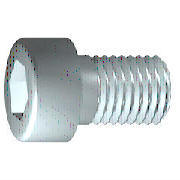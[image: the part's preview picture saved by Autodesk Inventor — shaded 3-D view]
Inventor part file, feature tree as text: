
AUTODESK INVENTOR PART (.ipt)
format: ipt  version: 2020 (Build 240168000, 168)  size: 191,488 bytes
history: native  units: mm (DEFAULTED — no unit token found)
features: sketch x2, extrude x1, plane x1, fillet x1
ambient origin geometry x7: Origin, YZ Plane, XY Plane, X Axis, Y Axis, Z Axis, Center Point
bodies: Solid1 (feature_tree), Body (feature_tree)
feature tree (5):
  extrude  "Slot"  Depth=3.0mm
  plane  "Work Plane1"
  fillet  "Fillet2"  Radius=3.0mm
  sketch  "Sketch1"  dims[d1=18.75mm d2=0.306825mm d3=3.0mm]
  sketch  "Sketch2"  dims[d4=1.3mm d5=60.0deg d6=3.0mm d7=3.0mm d8=2.886751mm d9=5.5mm d10=90.0deg d11=10.0mm d12=0.0mm d13=18.75mm d14=0.0mm d15=0.306725mm d16=0.306725mm d17=0.3mm d19=0.0mm d26=20.0mm d27=45.0deg d28=0.0mm d29=0.0mm d30=0.1mm]
